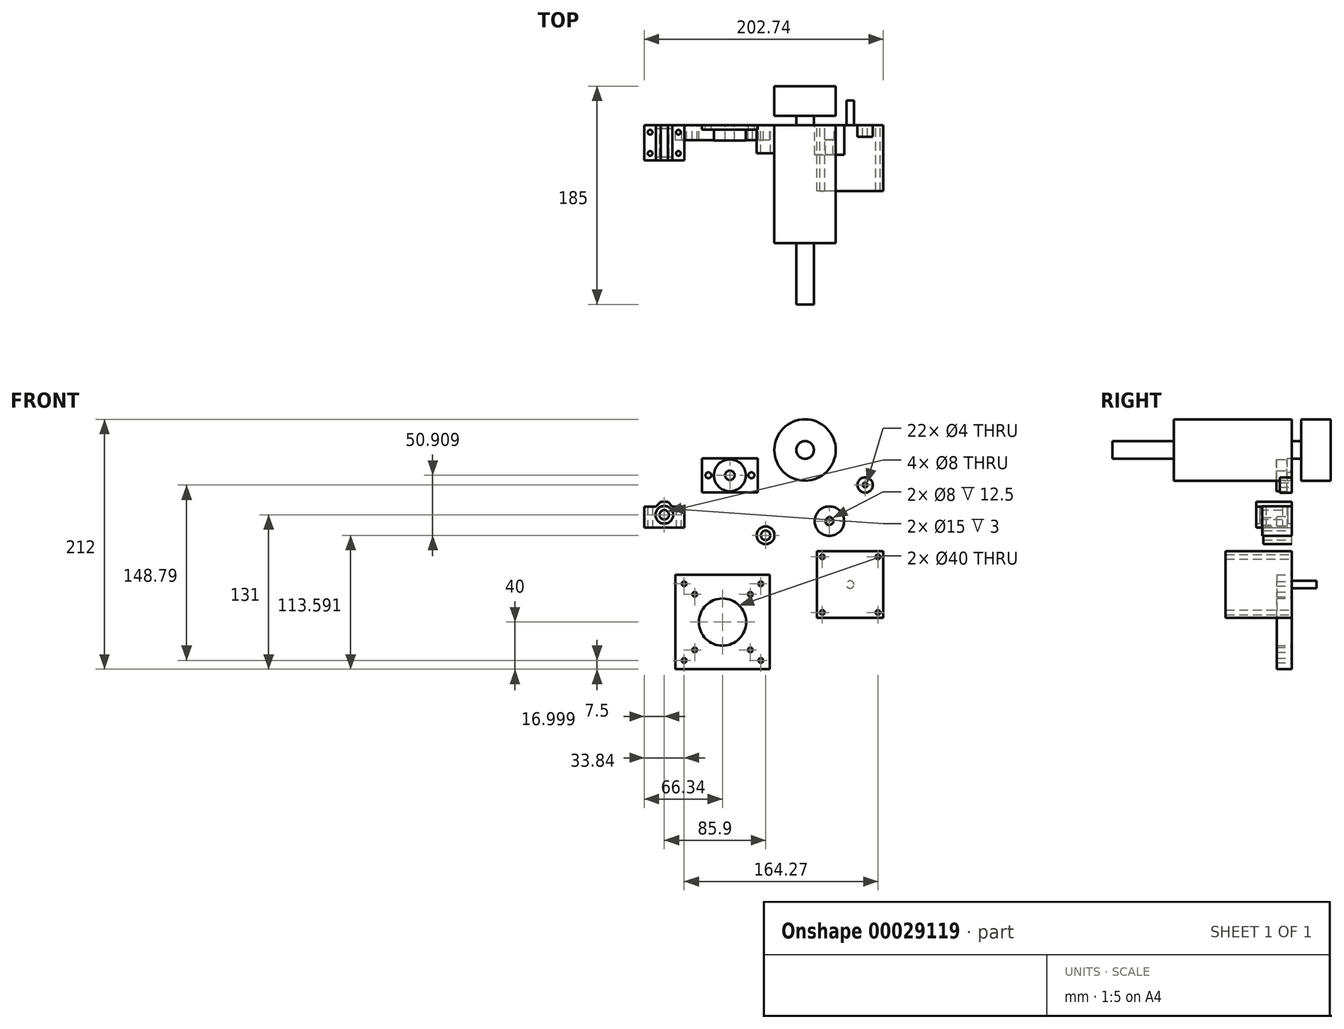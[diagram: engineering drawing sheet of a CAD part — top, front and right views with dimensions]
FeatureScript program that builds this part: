
annotation { "Feature Type Name" : "Feature", "Feature Type Description" : "" }
export const myFeature = defineFeature(function(context is Context, id is Id, definition is map)
    precondition{}
    {
        {
            var Q0;
            Q0=qCreatedBy(makeId("Front.planeOp"),FACE);
            var sketch = newSketch(context, id + "F0", { "sketchPlane" : qUnion([Q0])});
            skCircle(sketch, "E0", {"center": v(-33.44, 3.6) * mm, "radius": 7.5 * mm});
            skCircle(sketch, "E1", {"center": v(-33.44, 3.6) * mm, "radius": 4 * mm});
            skSolve(sketch);
        }
        {
            var Q0;
            Q0=makeQuery(id+"F0.imprint","IMPRINT",FACE,{"disambiguationData":[TD([[makeQuery(id+"F0.imprint","IMPRINT",EDGE,{"derivedFrom":sQuery(id+"F0.wireOp",EDGE,"E0")}),1.0]])]});
            extrude(context, id + "F1", {"entities" : qUnion([Q0]), "depth" : 24 * mm});
        }
        {
            var Q0;
            Q0=qCreatedBy(makeId("Right.planeOp"),FACE);
            var sketch = newSketch(context, id + "F2", { "sketchPlane" : qUnion([Q0])});
            skLineSegment(sketch, "E2", {"start": v(-152, 83.5) * mm, "end": v(-100, 83.5) * mm});
            skLineSegment(sketch, "E3", {"start": v(-100, 83.5) * mm, "end": v(-100, 102) * mm});
            skLineSegment(sketch, "E4", {"start": v(-100, 102) * mm, "end": v(0, 102) * mm});
            skLineSegment(sketch, "E5", {"start": v(0, 102) * mm, "end": v(0, 83.5) * mm});
            skLineSegment(sketch, "E6", {"start": v(0, 83.5) * mm, "end": v(8, 83.5) * mm});
            skLineSegment(sketch, "E7", {"start": v(8, 83.5) * mm, "end": v(8, 102) * mm});
            skLineSegment(sketch, "E8", {"start": v(8, 102) * mm, "end": v(33, 102) * mm});
            skLineSegment(sketch, "E9", {"start": v(-152, 76) * mm, "end": v(33, 76) * mm});
            skLineSegment(sketch, "E10", {"start": v(-152, 83.5) * mm, "end": v(-152, 76) * mm});
            skLineSegment(sketch, "E11", {"start": v(33, 76) * mm, "end": v(33, 102) * mm});
            skSolve(sketch);
        }
        {
            var Q0;
            Q0=makeQuery(id+"F2.imprint","IMPRINT",FACE,{"disambiguationData":[TD([[makeQuery(id+"F2.imprint","IMPRINT",EDGE,{"derivedFrom":sQuery(id+"F2.wireOp",EDGE,"E2")}),-1.0]])]});
            var Q1;
            Q1=sQuery(id+"F2.wireOp",EDGE,"E10");
            var Q2;
            Q2=sQuery(id+"F2.wireOp",EDGE,"E2");
            var Q3;
            Q3=sQuery(id+"F2.wireOp",EDGE,"E3");
            var Q4;
            Q4=sQuery(id+"F2.wireOp",EDGE,"E4");
            var Q5;
            Q5=sQuery(id+"F2.wireOp",EDGE,"E5");
            var Q6;
            Q6=sQuery(id+"F2.wireOp",EDGE,"E6");
            var Q7;
            Q7=sQuery(id+"F2.wireOp",EDGE,"E7");
            var Q8;
            Q8=sQuery(id+"F2.wireOp",EDGE,"E8");
            var Q9;
            Q9=sQuery(id+"F2.wireOp",EDGE,"E11");
            var Q10;
            Q10=sQuery(id+"F2.wireOp",EDGE,"E9");
            revolve(context, id + "F3", {"entities" : qUnion([Q0]), "surfaceEntities" : qUnion([Q1, Q2, Q3, Q4, Q5, Q6, Q7, Q8, Q9]), "axis" : qUnion([Q10]), "revolveType" : RevolveType.FULL});
        }
        {
            var Q0;
            Q0=qCreatedBy(makeId("Front.planeOp"),FACE);
            var sketch = newSketch(context, id + "F4", { "sketchPlane" : qUnion([Q0])});
            skCircle(sketch, "E12", {"center": v(20.64, 15.62) * mm, "radius": 12.5 * mm});
            skCircle(sketch, "E13", {"center": v(20.64, 15.62) * mm, "radius": 3.18 * mm});
            skCircle(sketch, "E14", {"center": v(20.64, 15.62) * mm, "radius": 4 * mm});
            skSolve(sketch);
        }
        {
            var Q0;
            Q0=makeQuery(id+"F4.imprint","IMPRINT",FACE,{"disambiguationData":[TD([[makeQuery(id+"F4.imprint","IMPRINT",EDGE,{"derivedFrom":sQuery(id+"F4.wireOp",EDGE,"E12")}),1.0]])]});
            var Q1;
            Q1=makeQuery(id+"F4.imprint","IMPRINT",FACE,{"disambiguationData":[TD([[makeQuery(id+"F4.imprint","IMPRINT",EDGE,{"derivedFrom":sQuery(id+"F4.wireOp",EDGE,"E13")}),1.0]])]});
            var Q2;
            Q2=makeQuery(id+"F4.imprint","IMPRINT",FACE,{"disambiguationData":[TD([[makeQuery(id+"F4.imprint","IMPRINT",EDGE,{"derivedFrom":sQuery(id+"F4.wireOp",EDGE,"E13")}),-1.0]])]});
            extrude(context, id + "F5", {"entities" : qUnion([Q0, Q1, Q2]), "depth" : 25 * mm});
        }
        {
            var Q0;
            Q0=makeQuery(id+"F4.imprint","IMPRINT",FACE,{"disambiguationData":[TD([[makeQuery(id+"F4.imprint","IMPRINT",EDGE,{"derivedFrom":sQuery(id+"F4.wireOp",EDGE,"E13")}),1.0]])]});
            extrude(context, id + "F6", {"entities" : qUnion([Q0]), "operationType" : NewBodyOperationType.REMOVE, "endBound" : BoundingType.UP_TO_NEXT, "depth" : 25 * mm});
        }
        {
            var Q0;
            Q0=makeQuery(id+"F4.imprint","IMPRINT",FACE,{"disambiguationData":[TD([[makeQuery(id+"F4.imprint","IMPRINT",EDGE,{"derivedFrom":sQuery(id+"F4.wireOp",EDGE,"E13")}),-1.0]])]});
            extrude(context, id + "F7", {"entities" : qUnion([Q0]), "operationType" : NewBodyOperationType.REMOVE, "depth" : 12.5 * mm});
        }
        {
            var Q0;
            Q0=qCreatedBy(makeId("Front.planeOp"),FACE);
            var sketch = newSketch(context, id + "F8", { "sketchPlane" : qUnion([Q0])});
            skLineSegment(sketch, "E15.bottom", {"start": v(66.4, -10) * mm, "end": v(10, -10) * mm});
            skLineSegment(sketch, "E15.top", {"start": v(66.4, -66.4) * mm, "end": v(10, -66.4) * mm});
            skLineSegment(sketch, "E15.left", {"start": v(66.4, -10) * mm, "end": v(66.4, -66.4) * mm});
            skLineSegment(sketch, "E15.right", {"start": v(10, -10) * mm, "end": v(10, -66.4) * mm});
            skCircle(sketch, "E16", {"center": v(61.77, -14.63) * mm, "radius": 2 * mm});
            skCircle(sketch, "E17.0.1.0", {"center": v(61.77, -61.77) * mm, "radius": 2 * mm});
            skCircle(sketch, "E17.1.0.0", {"center": v(14.63, -14.63) * mm, "radius": 2 * mm});
            skCircle(sketch, "E17.1.1.0", {"center": v(14.63, -61.77) * mm, "radius": 2 * mm});
            skLineSegment(sketch, "E17.direction1", {"start": v(61.77, -14.63) * mm, "end": v(14.63, -14.63) * mm, "construction": true});
            skLineSegment(sketch, "E17.direction2", {"start": v(61.77, -14.63) * mm, "end": v(61.77, -61.77) * mm, "construction": true});
            skLineSegment(sketch, "E18", {"start": v(61.77, -61.77) * mm, "end": v(14.63, -14.63) * mm, "construction": true});
            skLineSegment(sketch, "E19", {"start": v(61.77, -14.63) * mm, "end": v(14.63, -61.77) * mm, "construction": true});
            skPoint(sketch, "E20", {"position": v(38.2, -38.2) * mm});
            skLineSegment(sketch, "E21", {"start": v(10, -10) * mm, "end": v(66.4, -66.4) * mm, "construction": true});
            skLineSegment(sketch, "E22", {"start": v(66.4, -10) * mm, "end": v(10, -66.4) * mm, "construction": true});
            skCircle(sketch, "E23", {"center": v(38.2, -38.2) * mm, "radius": 3.18 * mm});
            skSolve(sketch);
        }
        {
            var Q0;
            Q0=makeQuery(id+"F8.imprint","IMPRINT",FACE,{"disambiguationData":[TD([[makeQuery(id+"F8.imprint","IMPRINT",EDGE,{"derivedFrom":sQuery(id+"F8.wireOp",EDGE,"E15.bottom")}),1.0]])]});
            var Q1;
            Q1=makeQuery(id+"F8.imprint","IMPRINT",FACE,{"disambiguationData":[TD([[makeQuery(id+"F8.imprint","IMPRINT",EDGE,{"derivedFrom":sQuery(id+"F8.wireOp",EDGE,"E23")}),1.0]])]});
            extrude(context, id + "F9", {"entities" : qUnion([Q0, Q1]), "depth" : 56 * mm});
        }
        {
            var Q0;
            Q0=makeQuery(id+"F8.imprint","IMPRINT",FACE,{"disambiguationData":[TD([[makeQuery(id+"F8.imprint","IMPRINT",EDGE,{"derivedFrom":sQuery(id+"F8.wireOp",EDGE,"E23")}),1.0]])]});
            extrude(context, id + "F10", {"entities" : qUnion([Q0]), "operationType" : NewBodyOperationType.ADD, "oppositeDirection" : true, "depth" : 21 * mm});
        }
        {
            var Q0;
            Q0=qCreatedBy(makeId("Front.planeOp"),FACE);
            var sketch = newSketch(context, id + "F11", { "sketchPlane" : qUnion([Q0])});
            skLineSegment(sketch, "E24.bottom", {"start": v(-87.5, 69) * mm, "end": v(-40, 69) * mm});
            skLineSegment(sketch, "E24.top", {"start": v(-87.5, 40) * mm, "end": v(-40, 40) * mm});
            skLineSegment(sketch, "E24.left", {"start": v(-87.5, 69) * mm, "end": v(-87.5, 40) * mm});
            skLineSegment(sketch, "E24.right", {"start": v(-40, 69) * mm, "end": v(-40, 40) * mm});
            skLineSegment(sketch, "E25", {"start": v(-87.5, 69) * mm, "end": v(-40, 40) * mm, "construction": true});
            skLineSegment(sketch, "E26", {"start": v(-40, 69) * mm, "end": v(-87.5, 40) * mm, "construction": true});
            skPoint(sketch, "E27", {"position": v(-63.75, 54.5) * mm});
            skCircle(sketch, "E28", {"center": v(-63.75, 54.5) * mm, "radius": 4 * mm});
            skCircle(sketch, "E29", {"center": v(-63.75, 54.5) * mm, "radius": 13.5 * mm});
            skLineSegment(sketch, "E30", {"start": v(-87.5, 54.5) * mm, "end": v(-40, 54.5) * mm, "construction": true});
            skCircle(sketch, "E31", {"center": v(-82, 54.5) * mm, "radius": 2.5 * mm});
            skCircle(sketch, "E32", {"center": v(-45.5, 54.5) * mm, "radius": 2.5 * mm});
            skSolve(sketch);
        }
        {
            var Q0;
            Q0=makeQuery(id+"F11.imprint","IMPRINT",FACE,{"disambiguationData":[TD([[makeQuery(id+"F11.imprint","IMPRINT",EDGE,{"derivedFrom":sQuery(id+"F11.wireOp",EDGE,"E24.bottom")}),-1.0]])]});
            extrude(context, id + "F12", {"entities" : qUnion([Q0]), "depth" : 4 * mm});
        }
        {
            var Q0;
            Q0=makeQuery(id+"F11.imprint","IMPRINT",FACE,{"disambiguationData":[TD([[makeQuery(id+"F11.imprint","IMPRINT",EDGE,{"derivedFrom":sQuery(id+"F11.wireOp",EDGE,"E28")}),-1.0]])]});
            extrude(context, id + "F13", {"entities" : qUnion([Q0]), "operationType" : NewBodyOperationType.ADD, "depth" : 13 * mm});
        }
        {
            var Q0;
            Q0=qCreatedBy(makeId("Front.planeOp"),FACE);
            var sketch = newSketch(context, id + "F14", { "sketchPlane" : qUnion([Q0])});
            skLineSegment(sketch, "E33.bottom", {"start": v(-30, -30) * mm, "end": v(-110, -30) * mm});
            skLineSegment(sketch, "E33.top", {"start": v(-30, -110) * mm, "end": v(-110, -110) * mm});
            skLineSegment(sketch, "E33.left", {"start": v(-30, -30) * mm, "end": v(-30, -110) * mm});
            skLineSegment(sketch, "E33.right", {"start": v(-110, -30) * mm, "end": v(-110, -110) * mm});
            skLineSegment(sketch, "E34", {"start": v(-30, -30) * mm, "end": v(-110, -110) * mm, "construction": true});
            skLineSegment(sketch, "E35", {"start": v(-110, -30) * mm, "end": v(-30, -110) * mm, "construction": true});
            skPoint(sketch, "E36", {"position": v(-70, -70) * mm});
            skCircle(sketch, "E37", {"center": v(-70, -70) * mm, "radius": 20 * mm});
            skCircle(sketch, "E38", {"center": v(-46.43, -46.43) * mm, "radius": 2 * mm});
            skCircle(sketch, "E39.0.1.0", {"center": v(-46.43, -93.57) * mm, "radius": 2 * mm});
            skCircle(sketch, "E39.1.0.0", {"center": v(-93.57, -46.43) * mm, "radius": 2 * mm});
            skCircle(sketch, "E39.1.1.0", {"center": v(-93.57, -93.57) * mm, "radius": 2 * mm});
            skLineSegment(sketch, "E39.direction1", {"start": v(-46.43, -46.43) * mm, "end": v(-93.57, -46.43) * mm, "construction": true});
            skLineSegment(sketch, "E39.direction2", {"start": v(-46.43, -46.43) * mm, "end": v(-46.43, -93.57) * mm, "construction": true});
            skLineSegment(sketch, "E40", {"start": v(-46.43, -93.57) * mm, "end": v(-93.57, -46.43) * mm, "construction": true});
            skLineSegment(sketch, "E41", {"start": v(-46.43, -46.43) * mm, "end": v(-93.57, -93.57) * mm, "construction": true});
            skCircle(sketch, "E42", {"center": v(-102.5, -102.5) * mm, "radius": 2 * mm});
            skCircle(sketch, "E43.0.1.0", {"center": v(-102.5, -37.5) * mm, "radius": 2 * mm});
            skCircle(sketch, "E43.1.0.0", {"center": v(-37.5, -102.5) * mm, "radius": 2 * mm});
            skCircle(sketch, "E43.1.1.0", {"center": v(-37.5, -37.5) * mm, "radius": 2 * mm});
            skLineSegment(sketch, "E43.direction1", {"start": v(-102.5, -102.5) * mm, "end": v(-37.5, -102.5) * mm, "construction": true});
            skLineSegment(sketch, "E43.direction2", {"start": v(-102.5, -102.5) * mm, "end": v(-102.5, -37.5) * mm, "construction": true});
            skLineSegment(sketch, "E44", {"start": v(-37.5, -37.5) * mm, "end": v(-102.5, -102.5) * mm, "construction": true});
            skLineSegment(sketch, "E45", {"start": v(-37.5, -102.5) * mm, "end": v(-102.5, -37.5) * mm, "construction": true});
            skSolve(sketch);
        }
        {
            var Q0;
            Q0=makeQuery(id+"F14.imprint","IMPRINT",FACE,{"disambiguationData":[TD([[makeQuery(id+"F14.imprint","IMPRINT",EDGE,{"derivedFrom":sQuery(id+"F14.wireOp",EDGE,"E33.bottom")}),1.0]])]});
            extrude(context, id + "F15", {"entities" : qUnion([Q0]), "depth" : 12.7 * mm});
        }
        {
            var Q0;
            Q0=qCreatedBy(makeId("Front.planeOp"),FACE);
            var sketch = newSketch(context, id + "F16", { "sketchPlane" : qUnion([Q0])});
            skCircle(sketch, "E46", {"center": v(50.92, 46.29) * mm, "radius": 2 * mm});
            skCircle(sketch, "E47", {"center": v(50.92, 46.29) * mm, "radius": 6.5 * mm});
            skSolve(sketch);
        }
        {
            var Q0;
            Q0=makeQuery(id+"F16.imprint","IMPRINT",FACE,{"disambiguationData":[TD([[makeQuery(id+"F16.imprint","IMPRINT",EDGE,{"derivedFrom":sQuery(id+"F16.wireOp",EDGE,"E46")}),-1.0]])]});
            extrude(context, id + "F17", {"entities" : qUnion([Q0]), "depth" : 10 * mm});
        }
        {
            var Q0;
            Q0=qCreatedBy(makeId("Front.planeOp"),FACE);
            var sketch = newSketch(context, id + "F18", { "sketchPlane" : qUnion([Q0])});
            skLineSegment(sketch, "E48.top", {"start": v(-136.34, 10) * mm, "end": v(-102.34, 10) * mm});
            skLineSegment(sketch, "E49", {"start": v(-136.34, 28) * mm, "end": v(-126.34, 28) * mm});
            skLineSegment(sketch, "E50", {"start": v(-126.34, 28) * mm, "end": v(-122.34, 32) * mm});
            skLineSegment(sketch, "E51", {"start": v(-122.34, 32) * mm, "end": v(-116.34, 32) * mm});
            skLineSegment(sketch, "E52", {"start": v(-116.34, 32) * mm, "end": v(-112.34, 28) * mm});
            skLineSegment(sketch, "E53", {"start": v(-112.34, 28) * mm, "end": v(-102.34, 28) * mm});
            skLineSegment(sketch, "E54", {"start": v(-136.34, 28) * mm, "end": v(-136.34, 10) * mm});
            skLineSegment(sketch, "E55", {"start": v(-102.34, 28) * mm, "end": v(-102.34, 10) * mm});
            skLineSegment(sketch, "E56", {"start": v(-119.34, 32) * mm, "end": v(-119.34, 10) * mm, "construction": true});
            skCircle(sketch, "E57", {"center": v(-119.34, 21) * mm, "radius": 7.5 * mm});
            skCircle(sketch, "E58", {"center": v(-119.34, 21) * mm, "radius": 4 * mm});
            skSolve(sketch);
        }
        {
            var Q0;
            Q0 = qSketchRegion(id + "F18", true);
            extrude(context, id + "F19", {"entities" : qUnion([Q0]), "depth" : 30 * mm});
        }
        {
            var Q0;
            Q0=makeQuery(id+"F18.imprint","IMPRINT",FACE,{"disambiguationData":[TD([[makeQuery(id+"F18.imprint","IMPRINT",EDGE,{"derivedFrom":sQuery(id+"F18.wireOp",EDGE,"E57")}),1.0]])]});
            extrude(context, id + "F20", {"entities" : qUnion([Q0]), "operationType" : NewBodyOperationType.ADD, "depth" : 27 * mm, "hasSecondDirection" : true, "secondDirectionOppositeDirection" : false, "secondDirectionDepth" : 3 * mm});
        }
        {
            var Q0;
            Q0=makeQuery(id+"F19.opExtrude","SWEPT_FACE",FACE,{"disambiguationData":[OSD([sQuery(id+"F18.wireOp",EDGE,"E48.top")])]});
            var sketch = newSketch(context, id + "F21", { "sketchPlane" : qUnion([Q0])});
            skCircle(sketch, "E59", {"center": v(-131.34, 24) * mm, "radius": 2 * mm});
            skCircle(sketch, "E60.0.1.0", {"center": v(-131.34, 6) * mm, "radius": 2 * mm});
            skCircle(sketch, "E60.1.0.0", {"center": v(-107.34, 24) * mm, "radius": 2 * mm});
            skCircle(sketch, "E60.1.1.0", {"center": v(-107.34, 6) * mm, "radius": 2 * mm});
            skLineSegment(sketch, "E60.direction1", {"start": v(-131.34, 24) * mm, "end": v(-107.34, 24) * mm, "construction": true});
            skLineSegment(sketch, "E60.direction2", {"start": v(-131.34, 24) * mm, "end": v(-131.34, 6) * mm, "construction": true});
            skLineSegment(sketch, "E61", {"start": v(-107.34, 6) * mm, "end": v(-131.34, 24) * mm, "construction": true});
            skLineSegment(sketch, "E62", {"start": v(-102.34, 30) * mm, "end": v(-136.34, 0) * mm, "construction": true});
            skPoint(sketch, "E63", {"position": v(-119.34, 15) * mm});
            skSolve(sketch);
        }
        {
            var Q0;
            Q0=makeQuery(id+"F21.imprint","IMPRINT",FACE,{"disambiguationData":[TD([[makeQuery(id+"F21.imprint","IMPRINT",EDGE,{"derivedFrom":sQuery(id+"F21.wireOp",EDGE,"E59")}),1.0]])]});
            var Q1;
            Q1=makeQuery(id+"F21.imprint","IMPRINT",FACE,{"disambiguationData":[TD([[makeQuery(id+"F21.imprint","IMPRINT",EDGE,{"derivedFrom":sQuery(id+"F21.wireOp",EDGE,"E60.1.0.0")}),1.0]])]});
            var Q2;
            Q2=makeQuery(id+"F21.imprint","IMPRINT",FACE,{"disambiguationData":[TD([[makeQuery(id+"F21.imprint","IMPRINT",EDGE,{"derivedFrom":sQuery(id+"F21.wireOp",EDGE,"E60.1.1.0")}),1.0]])]});
            var Q3;
            Q3=makeQuery(id+"F21.imprint","IMPRINT",FACE,{"disambiguationData":[TD([[makeQuery(id+"F21.imprint","IMPRINT",EDGE,{"derivedFrom":sQuery(id+"F21.wireOp",EDGE,"E60.0.1.0")}),1.0]])]});
            extrude(context, id + "F22", {"entities" : qUnion([Q0, Q1, Q2, Q3]), "operationType" : NewBodyOperationType.REMOVE, "endBound" : BoundingType.UP_TO_NEXT, "oppositeDirection" : true, "depth" : 25 * mm});
        }
    });
